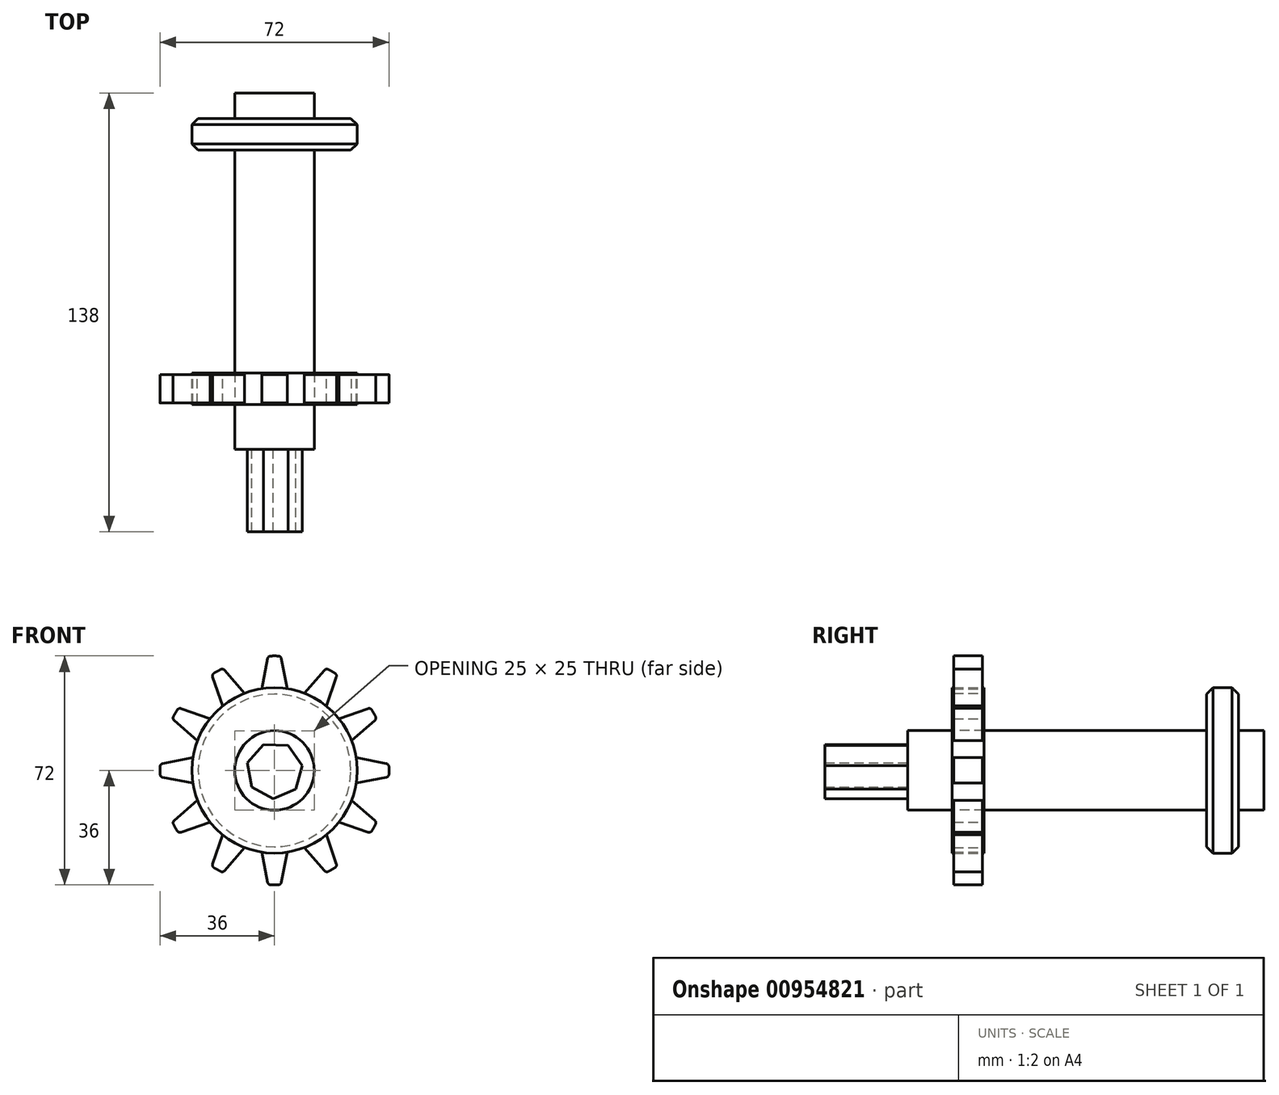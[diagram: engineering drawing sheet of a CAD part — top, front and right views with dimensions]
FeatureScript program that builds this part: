
annotation { "Feature Type Name" : "Feature", "Feature Type Description" : "" }
export const myFeature = defineFeature(function(context is Context, id is Id, definition is map)
    precondition{}
    {
        {
            var Q0;
            Q0=qCreatedBy(makeId("Front.planeOp"),FACE);
            var sketch = newSketch(context, id + "F0", { "sketchPlane" : qUnion([Q0])});
            skCircle(sketch, "E0", {"center": v(0, 0) * mm, "radius": 26 * mm});
            skSolve(sketch);
        }
        {
            var Q0;
            Q0=qSketchRegion(id+"F0",true);
            extrude(context, id + "F1", {"entities" : qUnion([Q0]), "depth" : 10 * mm, "offsetDistance" : 25 * mm});
        }
        {
            var Q0;
            Q0=qCreatedBy(makeId("Front.planeOp"),FACE);
            var Q1;
            Q1=makeQuery(id+"F1.opExtrude","CAP_FACE",FACE,{"disambiguationData":[OSD([sQuery(id+"F0.wireOp",EDGE,"E0")])],"isStart":false});
            cPlane(context, id + "F2", {"entities" : qUnion([Q0, Q1]), "cplaneType" : CPlaneType.MID_PLANE, "offset" : 25 * mm, "width" : 150 * mm, "height" : 150 * mm});
        }
        {
            var Q0;
            Q0=qCreatedBy(id+"F2.planeOp",FACE);
            var sketch = newSketch(context, id + "F3", { "sketchPlane" : qUnion([Q0])});
            skLineSegment(sketch, "E1", {"start": v(-25.7, -4) * mm, "end": v(-25.7, 4) * mm});
            skPoint(sketch, "E2.end.orphan", {"position": v(30.14, 4) * mm});
            skPoint(sketch, "E2.start.orphan", {"position": v(29.89, 0) * mm});
            skLineSegment(sketch, "E3", {"start": v(-25.7, 4) * mm, "end": v(-35.94, 2) * mm});
            skLineSegment(sketch, "E4", {"start": v(-25.7, -4) * mm, "end": v(-35.94, -2) * mm});
            skArc(sketch, "E5", {"start": v(-35.94, 2) * mm, "mid": v(-36, 0) * mm, "end": v(-35.94, -2) * mm, "construction": true});
            skArc(sketch, "E6", {"start": v(-35.94, 2) * mm, "mid": v(-36, 0) * mm, "end": v(-35.94, -2) * mm});
            skSolve(sketch);
        }
        {
            var Q0;
            Q0=makeQuery(id+"F3.imprint","IMPRINT",FACE,{"disambiguationData":[TD([[makeQuery(id+"F3.imprint","IMPRINT",EDGE,{"derivedFrom":sQuery(id+"F3.wireOp",EDGE,"E1")}),1.0]])]});
            extrude(context, id + "F4", {"entities" : qUnion([Q0]), "operationType" : NewBodyOperationType.ADD, "depth" : 9 * mm, "offsetDistance" : 25 * mm, "symmetric" : true});
        }
        {
            var Q0;
            Q0=makeQuery(id+"F4.opExtrude","SWEPT_EDGE",EDGE,{"disambiguationData":[OSD([sQuery(id+"F3.wireOp",EDGE,"E4"),sQuery(id+"F3.wireOp",EDGE,"E6")])]});
            var Q1;
            Q1=makeQuery(id+"F4.opExtrude","SWEPT_EDGE",EDGE,{"disambiguationData":[OSD([sQuery(id+"F3.wireOp",EDGE,"E3"),sQuery(id+"F3.wireOp",EDGE,"E6")])]});
            fillet(context, id + "F5", {"entities" : qUnion([Q0, Q1]), "radius" : 1 * mm, "tangentPropagation" : true, "allowEdgeOverflow" : false});
        }
        {
            var Q0;
            Q0=makeQuery(id+"F1.opExtrude","SWEPT_BODY",BODY,{"disambiguationData":[OSD([sQuery(id+"F0.wireOp",EDGE,"E0")])]});
            var Q1;
            Q1=makeQuery(id+"F1.opExtrude","CAP_EDGE",EDGE,{"disambiguationData":[OSD([sQuery(id+"F0.wireOp",EDGE,"E0")])],"isStart":true});
            circularPattern(context, id + "F6", {"entities" : qUnion([Q0]), "axis" : qUnion([Q1]), "angle" : 360 * degree, "instanceCount" : 12, "equalSpace" : true});
        }
        {
            var Q0;
            Q0=makeQuery(id+"F1.opExtrude","CAP_FACE",FACE,{"disambiguationData":[OSD([sQuery(id+"F0.wireOp",EDGE,"E0")])],"isStart":false});
            var sketch = newSketch(context, id + "F7", { "sketchPlane" : qUnion([Q0])});
            skCircle(sketch, "E7", {"center": v(0, 0) * mm, "radius": 12.5 * mm});
            skPoint(sketch, "E8.0.midPoint", {"position": v(7.03, 3.82) * mm});
            skPoint(sketch, "E9.orphan", {"position": v(4.82, 7.88) * mm});
            skPoint(sketch, "E8.0.end.orphan", {"position": v(9.23, -0.24) * mm});
            skSolve(sketch);
        }
        {
            var Q0;
            Q0=qSketchRegion(id+"F7",true);
            extrude(context, id + "F8", {"entities" : qUnion([Q0]), "oppositeDirection" : true, "depth" : 98 * mm, "offsetDistance" : 25 * mm});
        }
        {
            var Q0;
            Q0=makeQuery(id+"F8.opExtrude","CAP_FACE",FACE,{"disambiguationData":[OSD([sQuery(id+"F7.wireOp",EDGE,"E7")])],"isStart":true});
            extrude(context, id + "F9", {"entities" : qUnion([Q0]), "depth" : 14 * mm, "offsetDistance" : 25 * mm});
        }
        {
            var Q0;
            Q0=makeQuery(id+"F9.opExtrude","CAP_FACE",FACE,{"disambiguationData":[OSD([sQuery(id+"F7.wireOp",EDGE,"E7")])],"isStart":false});
            var sketch = newSketch(context, id + "F10", { "sketchPlane" : qUnion([Q0])});
            skCircle(sketch, "E10.cCircle", {"center": v(0, 0) * mm, "radius": 8 * mm, "construction": true});
            skLineSegment(sketch, "E10.0", {"start": v(4.23, 7.8) * mm, "end": v(8.74, 1.57) * mm});
            skLineSegment(sketch, "E10.1", {"start": v(8.74, 1.57) * mm, "end": v(6.67, -5.86) * mm});
            skLineSegment(sketch, "E10.2", {"start": v(6.67, -5.86) * mm, "end": v(-0.42, -8.87) * mm});
            skLineSegment(sketch, "E10.3", {"start": v(-0.42, -8.87) * mm, "end": v(-7.2, -5.2) * mm});
            skLineSegment(sketch, "E10.4", {"start": v(-7.2, -5.2) * mm, "end": v(-8.55, 2.38) * mm});
            skLineSegment(sketch, "E10.5", {"start": v(-8.55, 2.38) * mm, "end": v(-3.47, 8.17) * mm});
            skLineSegment(sketch, "E10.6", {"start": v(-3.47, 8.17) * mm, "end": v(4.23, 7.8) * mm});
            skPoint(sketch, "E10.0.midPoint", {"position": v(6.48, 4.69) * mm});
            skSolve(sketch);
        }
        {
            var Q0;
            Q0=makeQuery(id+"F10.imprint","IMPRINT",FACE,{"disambiguationData":[TD([[makeQuery(id+"F10.imprint","IMPRINT",EDGE,{"derivedFrom":sQuery(id+"F10.wireOp",EDGE,"E10.0")}),-1.0]])]});
            extrude(context, id + "F11", {"entities" : qUnion([Q0]), "operationType" : NewBodyOperationType.ADD, "depth" : 26 * mm, "offsetDistance" : 25 * mm});
        }
        {
            var Q0;
            Q0=makeQuery(id+"F8.opExtrude","CAP_FACE",FACE,{"disambiguationData":[OSD([sQuery(id+"F7.wireOp",EDGE,"E7")])],"isStart":false});
            cPlane(context, id + "F12", {"entities" : qUnion([Q0]), "cplaneType" : CPlaneType.OFFSET, "offset" : 13 * mm, "oppositeDirection" : true, "width" : 150 * mm, "height" : 150 * mm});
        }
        {
            var Q0;
            Q0=qCreatedBy(id+"F12.planeOp",FACE);
            var sketch = newSketch(context, id + "F13", { "sketchPlane" : qUnion([Q0])});
            skCircle(sketch, "E11", {"center": v(0, 0) * mm, "radius": 26 * mm});
            skSolve(sketch);
        }
        {
            var Q0;
            Q0=makeQuery(id+"F13.imprint","IMPRINT",FACE,{"disambiguationData":[TD([[makeQuery(id+"F13.imprint","IMPRINT",EDGE,{"derivedFrom":sQuery(id+"F13.wireOp",EDGE,"E11")}),1.0]])]});
            extrude(context, id + "F14", {"entities" : qUnion([Q0]), "operationType" : NewBodyOperationType.ADD, "depth" : 10 * mm, "offsetDistance" : 25 * mm, "symmetric" : true});
        }
        {
            var Q0;
            Q0=makeQuery(id+"F14.opExtrude","CAP_EDGE",EDGE,{"disambiguationData":[OSD([sQuery(id+"F13.wireOp",EDGE,"E11")])],"isStart":false});
            var Q1;
            Q1=makeQuery(id+"F14.opExtrude","CAP_EDGE",EDGE,{"disambiguationData":[OSD([sQuery(id+"F13.wireOp",EDGE,"E11")])],"isStart":true});
            chamfer(context, id + "F15", {"entities" : qUnion([Q0, Q1]), "width" : 2 * mm, "tangentPropagation" : true});
        }
    });
